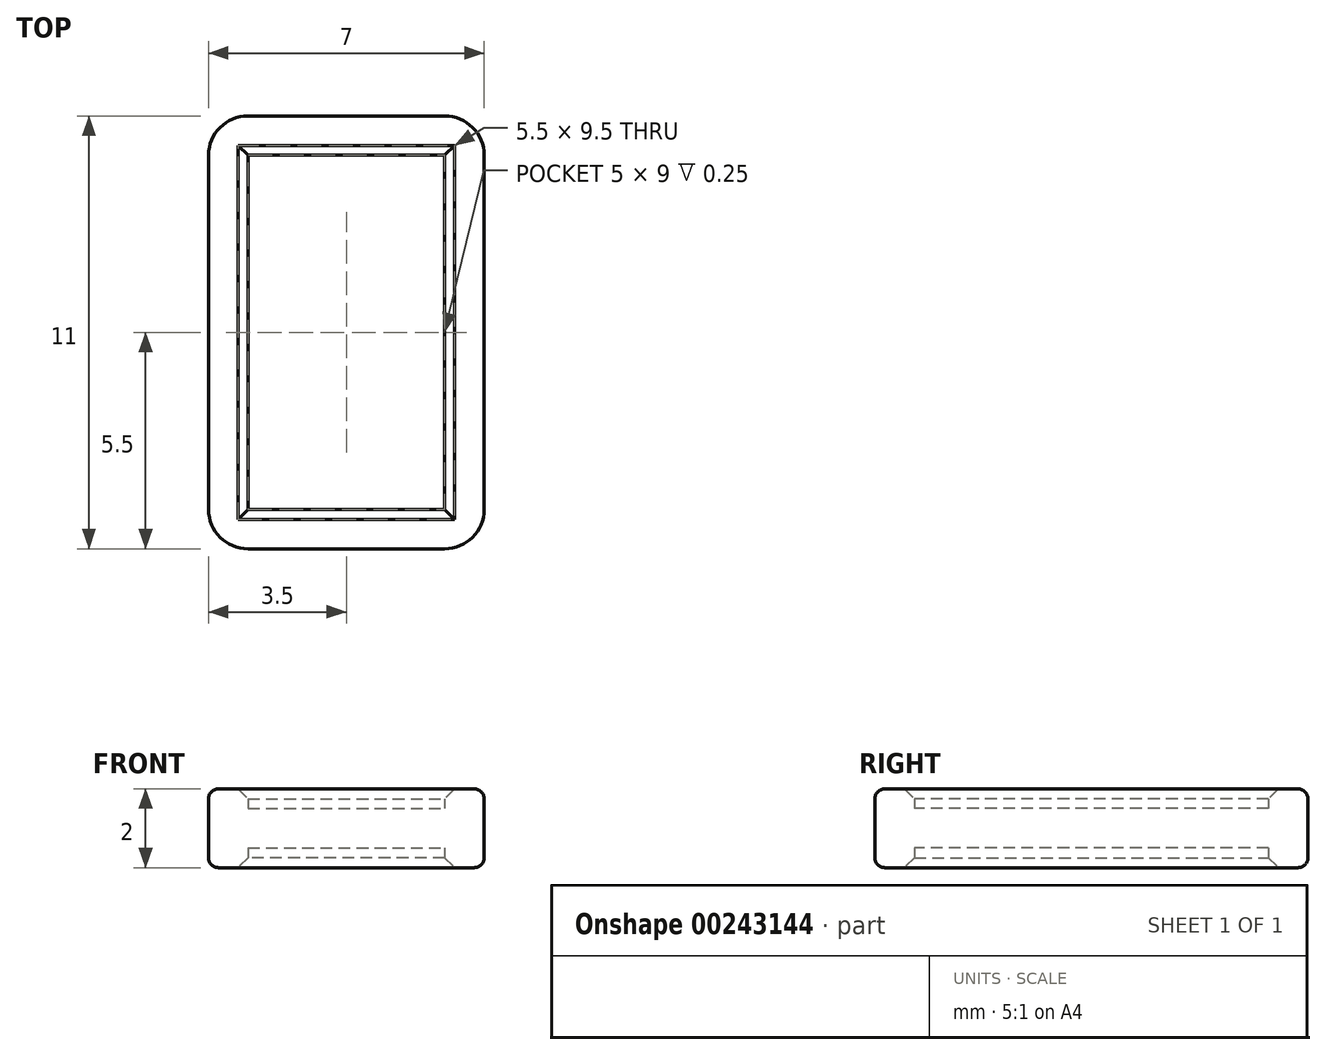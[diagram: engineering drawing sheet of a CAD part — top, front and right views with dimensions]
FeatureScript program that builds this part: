
annotation { "Feature Type Name" : "Feature", "Feature Type Description" : "" }
export const myFeature = defineFeature(function(context is Context, id is Id, definition is map)
    precondition{}
    {
        {
            var Q0;
            Q0=qCreatedBy(makeId("Top.planeOp"),FACE);
            var sketch = newSketch(context, id + "F0", { "sketchPlane" : qUnion([Q0])});
            skLineSegment(sketch, "E0.bottom", {"start": v(0, 0) * mm, "end": v(6, 0) * mm});
            skLineSegment(sketch, "E0.top", {"start": v(0, 10) * mm, "end": v(6, 10) * mm});
            skLineSegment(sketch, "E0.left", {"start": v(0, 0) * mm, "end": v(0, 10) * mm});
            skLineSegment(sketch, "E0.right", {"start": v(6, 0) * mm, "end": v(6, 10) * mm});
            skSolve(sketch);
        }
        {
            var Q0;
            Q0 = qSketchRegion(id + "F0", true);
            extrude(context, id + "F1", {"entities" : qUnion([Q0]), "depth" : 1 * mm});
        }
        {
            var Q0;
            Q0=makeQuery(id+"F1.opExtrude","SWEPT_EDGE",EDGE,{"disambiguationData":[OSD([sQuery(id+"F0.wireOp",EDGE,"E0.bottom"),sQuery(id+"F0.wireOp",EDGE,"E0.right")])]});
            var Q1;
            Q1=makeQuery(id+"F1.opExtrude","SWEPT_EDGE",EDGE,{"disambiguationData":[OSD([sQuery(id+"F0.wireOp",EDGE,"E0.top"),sQuery(id+"F0.wireOp",EDGE,"E0.right")])]});
            var Q2;
            Q2=makeQuery(id+"F1.opExtrude","SWEPT_EDGE",EDGE,{"disambiguationData":[OSD([sQuery(id+"F0.wireOp",EDGE,"E0.bottom"),sQuery(id+"F0.wireOp",EDGE,"E0.left")])]});
            var Q3;
            Q3=makeQuery(id+"F1.opExtrude","SWEPT_EDGE",EDGE,{"disambiguationData":[OSD([sQuery(id+"F0.wireOp",EDGE,"E0.top"),sQuery(id+"F0.wireOp",EDGE,"E0.left")])]});
            fillet(context, id + "F2", {"entities" : qUnion([Q0, Q1, Q2, Q3]), "radius" : .5 * mm, "tangentPropagation" : true, "allowEdgeOverflow" : false});
        }
        {
            var Q0;
            Q0=qCreatedBy(makeId("Front.planeOp"),FACE);
            cPlane(context, id + "F3", {"entities" : qUnion([Q0]), "cplaneType" : CPlaneType.OFFSET, "offset" : .5 * mm, "oppositeDirection" : true, "width" : 150 * mm, "height" : 150 * mm});
        }
        {
            var Q0;
            Q0=qCreatedBy(id+"F3.planeOp",FACE);
            var sketch = newSketch(context, id + "F4", { "sketchPlane" : qUnion([Q0])});
            skLineSegment(sketch, "E1.0", {"start": v(6, 1) * mm, "end": v(6, 0) * mm});
            skLineSegment(sketch, "E1.1", {"start": v(5.5, 1) * mm, "end": v(6, 1) * mm});
            skLineSegment(sketch, "E1.2", {"start": v(6, 0) * mm, "end": v(5.5, 0) * mm});
            skLineSegment(sketch, "E2.0", {"start": v(6.5, -0.5) * mm, "end": v(5.5, -0.5) * mm});
            skLineSegment(sketch, "E2.1", {"start": v(6.5, 1.5) * mm, "end": v(6.5, -0.5) * mm});
            skLineSegment(sketch, "E2.2", {"start": v(5.5, 1.5) * mm, "end": v(6.5, 1.5) * mm});
            skLineSegment(sketch, "E3", {"start": v(5.5, 1.5) * mm, "end": v(5.5, 1) * mm});
            skLineSegment(sketch, "E4", {"start": v(5.5, 0) * mm, "end": v(5.5, -0.5) * mm});
            skSolve(sketch);
        }
        {
            var Q0;
            Q0=makeQuery(id+"F4.imprint","IMPRINT",FACE,{"disambiguationData":[TD([[makeQuery(id+"F4.imprint","IMPRINT",EDGE,{"derivedFrom":sQuery(id+"F4.wireOp",EDGE,"E1.0")}),1.0]])]});
            var Q1;
            Q1=makeQuery(id+"F1.opExtrude","CAP_EDGE",EDGE,{"disambiguationData":[OSD([sQuery(id+"F0.wireOp",EDGE,"E0.right")])],"isStart":false});
            var Q2;
            {var subQ0=sQuery(id+"F0.wireOp",EDGE,"E0.right");var subQ1=sQuery(id+"F0.wireOp",EDGE,"E0.top");Q2=makeQuery(id+"F2.opFillet","BLEND_EDGE",EDGE,{"blendedFrom":[makeQuery(id+"F1.opExtrude","SWEPT_EDGE",EDGE,{"disambiguationData":[OSD([subQ1,subQ0])]}),makeQuery(id+"F1.opExtrude","CAP_FACE",FACE,{"disambiguationData":[OSD([sQuery(id+"F0.wireOp",EDGE,"E0.bottom"),subQ1,sQuery(id+"F0.wireOp",EDGE,"E0.left"),subQ0])],"isStart":false})],"blendedInto":[makeQuery(id+"F1.opExtrude","CAP_FACE",FACE,{"disambiguationData":[OSD([sQuery(id+"F0.wireOp",EDGE,"E0.bottom"),subQ1,sQuery(id+"F0.wireOp",EDGE,"E0.left"),subQ0])],"isStart":false})]});}
            var Q3;
            Q3=makeQuery(id+"F1.opExtrude","CAP_EDGE",EDGE,{"disambiguationData":[OSD([sQuery(id+"F0.wireOp",EDGE,"E0.top")])],"isStart":false});
            var Q4;
            {var subQ0=sQuery(id+"F0.wireOp",EDGE,"E0.left");var subQ1=sQuery(id+"F0.wireOp",EDGE,"E0.top");Q4=makeQuery(id+"F2.opFillet","BLEND_EDGE",EDGE,{"blendedFrom":[makeQuery(id+"F1.opExtrude","SWEPT_EDGE",EDGE,{"disambiguationData":[OSD([subQ1,subQ0])]}),makeQuery(id+"F1.opExtrude","CAP_FACE",FACE,{"disambiguationData":[OSD([sQuery(id+"F0.wireOp",EDGE,"E0.bottom"),subQ1,subQ0,sQuery(id+"F0.wireOp",EDGE,"E0.right")])],"isStart":false})],"blendedInto":[makeQuery(id+"F1.opExtrude","CAP_FACE",FACE,{"disambiguationData":[OSD([sQuery(id+"F0.wireOp",EDGE,"E0.bottom"),subQ1,subQ0,sQuery(id+"F0.wireOp",EDGE,"E0.right")])],"isStart":false})]});}
            var Q5;
            Q5=makeQuery(id+"F1.opExtrude","CAP_EDGE",EDGE,{"disambiguationData":[OSD([sQuery(id+"F0.wireOp",EDGE,"E0.left")])],"isStart":false});
            var Q6;
            {var subQ0=sQuery(id+"F0.wireOp",EDGE,"E0.left");var subQ1=sQuery(id+"F0.wireOp",EDGE,"E0.bottom");Q6=makeQuery(id+"F2.opFillet","BLEND_EDGE",EDGE,{"blendedFrom":[makeQuery(id+"F1.opExtrude","SWEPT_EDGE",EDGE,{"disambiguationData":[OSD([subQ1,subQ0])]}),makeQuery(id+"F1.opExtrude","CAP_FACE",FACE,{"disambiguationData":[OSD([subQ1,sQuery(id+"F0.wireOp",EDGE,"E0.top"),subQ0,sQuery(id+"F0.wireOp",EDGE,"E0.right")])],"isStart":false})],"blendedInto":[makeQuery(id+"F1.opExtrude","CAP_FACE",FACE,{"disambiguationData":[OSD([subQ1,sQuery(id+"F0.wireOp",EDGE,"E0.top"),subQ0,sQuery(id+"F0.wireOp",EDGE,"E0.right")])],"isStart":false})]});}
            var Q7;
            Q7=makeQuery(id+"F1.opExtrude","CAP_EDGE",EDGE,{"disambiguationData":[OSD([sQuery(id+"F0.wireOp",EDGE,"E0.bottom")])],"isStart":false});
            var Q8;
            {var subQ0=sQuery(id+"F0.wireOp",EDGE,"E0.right");var subQ1=sQuery(id+"F0.wireOp",EDGE,"E0.bottom");Q8=makeQuery(id+"F2.opFillet","BLEND_EDGE",EDGE,{"blendedFrom":[makeQuery(id+"F1.opExtrude","SWEPT_EDGE",EDGE,{"disambiguationData":[OSD([subQ1,subQ0])]}),makeQuery(id+"F1.opExtrude","CAP_FACE",FACE,{"disambiguationData":[OSD([subQ1,sQuery(id+"F0.wireOp",EDGE,"E0.top"),sQuery(id+"F0.wireOp",EDGE,"E0.left"),subQ0])],"isStart":false})],"blendedInto":[makeQuery(id+"F1.opExtrude","CAP_FACE",FACE,{"disambiguationData":[OSD([subQ1,sQuery(id+"F0.wireOp",EDGE,"E0.top"),sQuery(id+"F0.wireOp",EDGE,"E0.left"),subQ0])],"isStart":false})]});}
            sweep(context, id + "F5", {"operationType" : NewBodyOperationType.ADD, "profiles" : qUnion([Q0]), "path" : qUnion([Q1, Q2, Q3, Q4, Q5, Q6, Q7, Q8])});
        }
        {
            var Q0;
            Q0=makeQuery(id+"F5.opSweep","SWEPT_EDGE",EDGE,{"disambiguationData":[OSD([sQuery(id+"F0.wireOp",EDGE,"E0.top"),sQuery(id+"F4.wireOp",EDGE,"E2.2"),sQuery(id+"F4.wireOp",EDGE,"E3")])]});
            var Q1;
            Q1=makeQuery(id+"F5.opSweep","SWEPT_EDGE",EDGE,{"disambiguationData":[OSD([sQuery(id+"F0.wireOp",EDGE,"E0.left"),sQuery(id+"F4.wireOp",EDGE,"E2.2"),sQuery(id+"F4.wireOp",EDGE,"E3")])]});
            var Q2;
            Q2=makeQuery(id+"F5.opSweep","SWEPT_EDGE",EDGE,{"disambiguationData":[OSD([sQuery(id+"F0.wireOp",EDGE,"E0.right"),sQuery(id+"F4.wireOp",EDGE,"E2.2"),sQuery(id+"F4.wireOp",EDGE,"E3")])]});
            var Q3;
            Q3=makeQuery(id+"F5.opSweep","SWEPT_EDGE",EDGE,{"disambiguationData":[OSD([sQuery(id+"F0.wireOp",EDGE,"E0.bottom"),sQuery(id+"F4.wireOp",EDGE,"E2.2"),sQuery(id+"F4.wireOp",EDGE,"E3")])]});
            var Q4;
            Q4=makeQuery(id+"F5.opSweep","SWEPT_EDGE",EDGE,{"disambiguationData":[OSD([sQuery(id+"F0.wireOp",EDGE,"E0.bottom"),sQuery(id+"F4.wireOp",EDGE,"E2.0"),sQuery(id+"F4.wireOp",EDGE,"E4")])]});
            var Q5;
            Q5=makeQuery(id+"F5.opSweep","SWEPT_EDGE",EDGE,{"disambiguationData":[OSD([sQuery(id+"F0.wireOp",EDGE,"E0.left"),sQuery(id+"F4.wireOp",EDGE,"E2.0"),sQuery(id+"F4.wireOp",EDGE,"E4")])]});
            var Q6;
            Q6=makeQuery(id+"F5.opSweep","SWEPT_EDGE",EDGE,{"disambiguationData":[OSD([sQuery(id+"F0.wireOp",EDGE,"E0.right"),sQuery(id+"F4.wireOp",EDGE,"E2.0"),sQuery(id+"F4.wireOp",EDGE,"E4")])]});
            var Q7;
            Q7=makeQuery(id+"F5.opSweep","SWEPT_EDGE",EDGE,{"disambiguationData":[OSD([sQuery(id+"F0.wireOp",EDGE,"E0.top"),sQuery(id+"F4.wireOp",EDGE,"E2.0"),sQuery(id+"F4.wireOp",EDGE,"E4")])]});
            chamfer(context, id + "F6", {"entities" : qUnion([Q0, Q1, Q2, Q3, Q4, Q5, Q6, Q7]), "width" : .25 * mm, "tangentPropagation" : true});
        }
        {
            var Q0;
            Q0=makeQuery(id+"F5.opSweep","SWEPT_EDGE",EDGE,{"disambiguationData":[OSD([sQuery(id+"F0.wireOp",EDGE,"E0.top"),sQuery(id+"F4.wireOp",EDGE,"E2.0"),sQuery(id+"F4.wireOp",EDGE,"E2.1")])]});
            var Q1;
            {var subQ0=sQuery(id+"F4.wireOp",EDGE,"E2.1");var subQ1=sQuery(id+"F4.wireOp",EDGE,"E2.0");var subQ2=sQuery(id+"F0.wireOp",EDGE,"E0.right");var subQ3=sQuery(id+"F0.wireOp",EDGE,"E0.left");var subQ4=sQuery(id+"F0.wireOp",EDGE,"E0.top");var subQ5=sQuery(id+"F0.wireOp",EDGE,"E0.bottom");Q1=makeQuery(id+"F5.opSweep","SWEPT_EDGE",EDGE,{"disambiguationData":[OSD([subQ5,subQ4,subQ3,subQ2,subQ1,subQ0]),TDD([makeQuery(id+"F2.opFillet","BLEND_EDGE",EDGE,{"blendedFrom":[makeQuery(id+"F1.opExtrude","SWEPT_EDGE",EDGE,{"disambiguationData":[OSD([subQ4,subQ2])]}),makeQuery(id+"F1.opExtrude","CAP_FACE",FACE,{"disambiguationData":[OSD([subQ5,subQ4,subQ3,subQ2])],"isStart":false})],"blendedInto":[makeQuery(id+"F1.opExtrude","CAP_FACE",FACE,{"disambiguationData":[OSD([subQ5,subQ4,subQ3,subQ2])],"isStart":false})]}),makeQuery(id+"F4.imprint","INTERSECT",VERTEX,{"derivedFrom":[subQ1,subQ0]})])]});}
            var Q2;
            Q2=makeQuery(id+"F5.opSweep","SWEPT_EDGE",EDGE,{"disambiguationData":[OSD([sQuery(id+"F0.wireOp",EDGE,"E0.right"),sQuery(id+"F4.wireOp",EDGE,"E2.0"),sQuery(id+"F4.wireOp",EDGE,"E2.1")])]});
            var Q3;
            {var subQ0=sQuery(id+"F4.wireOp",EDGE,"E2.1");var subQ1=sQuery(id+"F4.wireOp",EDGE,"E2.0");var subQ2=sQuery(id+"F0.wireOp",EDGE,"E0.right");var subQ3=sQuery(id+"F0.wireOp",EDGE,"E0.left");var subQ4=sQuery(id+"F0.wireOp",EDGE,"E0.top");var subQ5=sQuery(id+"F0.wireOp",EDGE,"E0.bottom");Q3=makeQuery(id+"F5.opSweep","SWEPT_EDGE",EDGE,{"disambiguationData":[OSD([subQ5,subQ4,subQ3,subQ2,subQ1,subQ0]),TDD([makeQuery(id+"F2.opFillet","BLEND_EDGE",EDGE,{"blendedFrom":[makeQuery(id+"F1.opExtrude","SWEPT_EDGE",EDGE,{"disambiguationData":[OSD([subQ5,subQ2])]}),makeQuery(id+"F1.opExtrude","CAP_FACE",FACE,{"disambiguationData":[OSD([subQ5,subQ4,subQ3,subQ2])],"isStart":false})],"blendedInto":[makeQuery(id+"F1.opExtrude","CAP_FACE",FACE,{"disambiguationData":[OSD([subQ5,subQ4,subQ3,subQ2])],"isStart":false})]}),makeQuery(id+"F4.imprint","INTERSECT",VERTEX,{"derivedFrom":[subQ1,subQ0]})])]});}
            var Q4;
            Q4=makeQuery(id+"F5.opSweep","SWEPT_EDGE",EDGE,{"disambiguationData":[OSD([sQuery(id+"F0.wireOp",EDGE,"E0.bottom"),sQuery(id+"F4.wireOp",EDGE,"E2.0"),sQuery(id+"F4.wireOp",EDGE,"E2.1")])]});
            var Q5;
            {var subQ0=sQuery(id+"F4.wireOp",EDGE,"E2.1");var subQ1=sQuery(id+"F4.wireOp",EDGE,"E2.0");var subQ2=sQuery(id+"F0.wireOp",EDGE,"E0.right");var subQ3=sQuery(id+"F0.wireOp",EDGE,"E0.left");var subQ4=sQuery(id+"F0.wireOp",EDGE,"E0.top");var subQ5=sQuery(id+"F0.wireOp",EDGE,"E0.bottom");Q5=makeQuery(id+"F5.opSweep","SWEPT_EDGE",EDGE,{"disambiguationData":[OSD([subQ5,subQ4,subQ3,subQ2,subQ1,subQ0]),TDD([makeQuery(id+"F2.opFillet","BLEND_EDGE",EDGE,{"blendedFrom":[makeQuery(id+"F1.opExtrude","SWEPT_EDGE",EDGE,{"disambiguationData":[OSD([subQ5,subQ3])]}),makeQuery(id+"F1.opExtrude","CAP_FACE",FACE,{"disambiguationData":[OSD([subQ5,subQ4,subQ3,subQ2])],"isStart":false})],"blendedInto":[makeQuery(id+"F1.opExtrude","CAP_FACE",FACE,{"disambiguationData":[OSD([subQ5,subQ4,subQ3,subQ2])],"isStart":false})]}),makeQuery(id+"F4.imprint","INTERSECT",VERTEX,{"derivedFrom":[subQ1,subQ0]})])]});}
            var Q6;
            Q6=makeQuery(id+"F5.opSweep","SWEPT_EDGE",EDGE,{"disambiguationData":[OSD([sQuery(id+"F0.wireOp",EDGE,"E0.left"),sQuery(id+"F4.wireOp",EDGE,"E2.0"),sQuery(id+"F4.wireOp",EDGE,"E2.1")])]});
            var Q7;
            {var subQ0=sQuery(id+"F4.wireOp",EDGE,"E2.1");var subQ1=sQuery(id+"F4.wireOp",EDGE,"E2.0");var subQ2=sQuery(id+"F0.wireOp",EDGE,"E0.right");var subQ3=sQuery(id+"F0.wireOp",EDGE,"E0.left");var subQ4=sQuery(id+"F0.wireOp",EDGE,"E0.top");var subQ5=sQuery(id+"F0.wireOp",EDGE,"E0.bottom");Q7=makeQuery(id+"F5.opSweep","SWEPT_EDGE",EDGE,{"disambiguationData":[OSD([subQ5,subQ4,subQ3,subQ2,subQ1,subQ0]),TDD([makeQuery(id+"F2.opFillet","BLEND_EDGE",EDGE,{"blendedFrom":[makeQuery(id+"F1.opExtrude","SWEPT_EDGE",EDGE,{"disambiguationData":[OSD([subQ4,subQ3])]}),makeQuery(id+"F1.opExtrude","CAP_FACE",FACE,{"disambiguationData":[OSD([subQ5,subQ4,subQ3,subQ2])],"isStart":false})],"blendedInto":[makeQuery(id+"F1.opExtrude","CAP_FACE",FACE,{"disambiguationData":[OSD([subQ5,subQ4,subQ3,subQ2])],"isStart":false})]}),makeQuery(id+"F4.imprint","INTERSECT",VERTEX,{"derivedFrom":[subQ1,subQ0]})])]});}
            var Q8;
            {var subQ0=sQuery(id+"F4.wireOp",EDGE,"E2.2");var subQ1=sQuery(id+"F4.wireOp",EDGE,"E2.1");var subQ2=sQuery(id+"F0.wireOp",EDGE,"E0.right");var subQ3=sQuery(id+"F0.wireOp",EDGE,"E0.left");var subQ4=sQuery(id+"F0.wireOp",EDGE,"E0.top");var subQ5=sQuery(id+"F0.wireOp",EDGE,"E0.bottom");Q8=makeQuery(id+"F5.opSweep","SWEPT_EDGE",EDGE,{"disambiguationData":[OSD([subQ5,subQ4,subQ3,subQ2,subQ1,subQ0]),TDD([makeQuery(id+"F2.opFillet","BLEND_EDGE",EDGE,{"blendedFrom":[makeQuery(id+"F1.opExtrude","SWEPT_EDGE",EDGE,{"disambiguationData":[OSD([subQ4,subQ2])]}),makeQuery(id+"F1.opExtrude","CAP_FACE",FACE,{"disambiguationData":[OSD([subQ5,subQ4,subQ3,subQ2])],"isStart":false})],"blendedInto":[makeQuery(id+"F1.opExtrude","CAP_FACE",FACE,{"disambiguationData":[OSD([subQ5,subQ4,subQ3,subQ2])],"isStart":false})]}),makeQuery(id+"F4.imprint","INTERSECT",VERTEX,{"derivedFrom":[subQ1,subQ0]})])]});}
            var Q9;
            Q9=makeQuery(id+"F5.opSweep","SWEPT_EDGE",EDGE,{"disambiguationData":[OSD([sQuery(id+"F0.wireOp",EDGE,"E0.right"),sQuery(id+"F4.wireOp",EDGE,"E2.1"),sQuery(id+"F4.wireOp",EDGE,"E2.2")])]});
            var Q10;
            {var subQ0=sQuery(id+"F4.wireOp",EDGE,"E2.2");var subQ1=sQuery(id+"F4.wireOp",EDGE,"E2.1");var subQ2=sQuery(id+"F0.wireOp",EDGE,"E0.right");var subQ3=sQuery(id+"F0.wireOp",EDGE,"E0.left");var subQ4=sQuery(id+"F0.wireOp",EDGE,"E0.top");var subQ5=sQuery(id+"F0.wireOp",EDGE,"E0.bottom");Q10=makeQuery(id+"F5.opSweep","SWEPT_EDGE",EDGE,{"disambiguationData":[OSD([subQ5,subQ4,subQ3,subQ2,subQ1,subQ0]),TDD([makeQuery(id+"F2.opFillet","BLEND_EDGE",EDGE,{"blendedFrom":[makeQuery(id+"F1.opExtrude","SWEPT_EDGE",EDGE,{"disambiguationData":[OSD([subQ5,subQ2])]}),makeQuery(id+"F1.opExtrude","CAP_FACE",FACE,{"disambiguationData":[OSD([subQ5,subQ4,subQ3,subQ2])],"isStart":false})],"blendedInto":[makeQuery(id+"F1.opExtrude","CAP_FACE",FACE,{"disambiguationData":[OSD([subQ5,subQ4,subQ3,subQ2])],"isStart":false})]}),makeQuery(id+"F4.imprint","INTERSECT",VERTEX,{"derivedFrom":[subQ1,subQ0]})])]});}
            var Q11;
            Q11=makeQuery(id+"F5.opSweep","SWEPT_EDGE",EDGE,{"disambiguationData":[OSD([sQuery(id+"F0.wireOp",EDGE,"E0.top"),sQuery(id+"F4.wireOp",EDGE,"E2.1"),sQuery(id+"F4.wireOp",EDGE,"E2.2")])]});
            var Q12;
            Q12=makeQuery(id+"F5.opSweep","SWEPT_EDGE",EDGE,{"disambiguationData":[OSD([sQuery(id+"F0.wireOp",EDGE,"E0.left"),sQuery(id+"F4.wireOp",EDGE,"E2.1"),sQuery(id+"F4.wireOp",EDGE,"E2.2")])]});
            var Q13;
            {var subQ0=sQuery(id+"F4.wireOp",EDGE,"E2.2");var subQ1=sQuery(id+"F4.wireOp",EDGE,"E2.1");var subQ2=sQuery(id+"F0.wireOp",EDGE,"E0.right");var subQ3=sQuery(id+"F0.wireOp",EDGE,"E0.left");var subQ4=sQuery(id+"F0.wireOp",EDGE,"E0.top");var subQ5=sQuery(id+"F0.wireOp",EDGE,"E0.bottom");Q13=makeQuery(id+"F5.opSweep","SWEPT_EDGE",EDGE,{"disambiguationData":[OSD([subQ5,subQ4,subQ3,subQ2,subQ1,subQ0]),TDD([makeQuery(id+"F2.opFillet","BLEND_EDGE",EDGE,{"blendedFrom":[makeQuery(id+"F1.opExtrude","SWEPT_EDGE",EDGE,{"disambiguationData":[OSD([subQ4,subQ3])]}),makeQuery(id+"F1.opExtrude","CAP_FACE",FACE,{"disambiguationData":[OSD([subQ5,subQ4,subQ3,subQ2])],"isStart":false})],"blendedInto":[makeQuery(id+"F1.opExtrude","CAP_FACE",FACE,{"disambiguationData":[OSD([subQ5,subQ4,subQ3,subQ2])],"isStart":false})]}),makeQuery(id+"F4.imprint","INTERSECT",VERTEX,{"derivedFrom":[subQ1,subQ0]})])]});}
            var Q14;
            Q14=makeQuery(id+"F5.opSweep","SWEPT_EDGE",EDGE,{"disambiguationData":[OSD([sQuery(id+"F0.wireOp",EDGE,"E0.bottom"),sQuery(id+"F4.wireOp",EDGE,"E2.1"),sQuery(id+"F4.wireOp",EDGE,"E2.2")])]});
            var Q15;
            {var subQ0=sQuery(id+"F4.wireOp",EDGE,"E2.2");var subQ1=sQuery(id+"F4.wireOp",EDGE,"E2.1");var subQ2=sQuery(id+"F0.wireOp",EDGE,"E0.right");var subQ3=sQuery(id+"F0.wireOp",EDGE,"E0.left");var subQ4=sQuery(id+"F0.wireOp",EDGE,"E0.top");var subQ5=sQuery(id+"F0.wireOp",EDGE,"E0.bottom");Q15=makeQuery(id+"F5.opSweep","SWEPT_EDGE",EDGE,{"disambiguationData":[OSD([subQ5,subQ4,subQ3,subQ2,subQ1,subQ0]),TDD([makeQuery(id+"F2.opFillet","BLEND_EDGE",EDGE,{"blendedFrom":[makeQuery(id+"F1.opExtrude","SWEPT_EDGE",EDGE,{"disambiguationData":[OSD([subQ5,subQ3])]}),makeQuery(id+"F1.opExtrude","CAP_FACE",FACE,{"disambiguationData":[OSD([subQ5,subQ4,subQ3,subQ2])],"isStart":false})],"blendedInto":[makeQuery(id+"F1.opExtrude","CAP_FACE",FACE,{"disambiguationData":[OSD([subQ5,subQ4,subQ3,subQ2])],"isStart":false})]}),makeQuery(id+"F4.imprint","INTERSECT",VERTEX,{"derivedFrom":[subQ1,subQ0]})])]});}
            fillet(context, id + "F7", {"entities" : qUnion([Q0, Q1, Q2, Q3, Q4, Q5, Q6, Q7, Q8, Q9, Q10, Q11, Q12, Q13, Q14, Q15]), "radius" : .25 * mm, "tangentPropagation" : true, "allowEdgeOverflow" : false});
        }
    });
